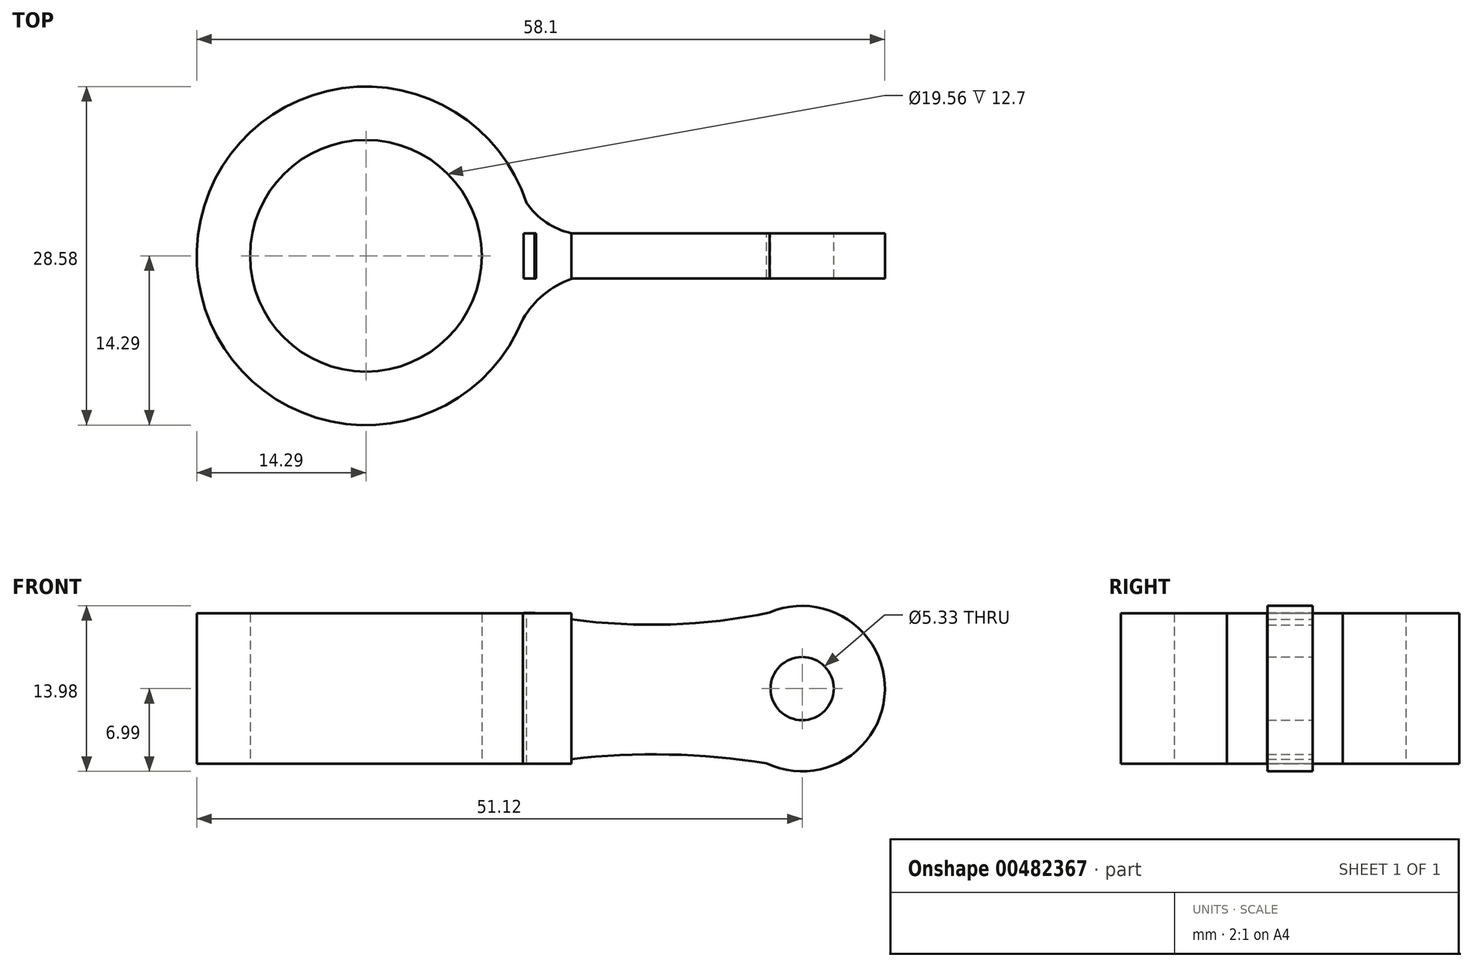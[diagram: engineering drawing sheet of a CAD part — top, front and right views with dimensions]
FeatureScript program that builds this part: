
annotation { "Feature Type Name" : "Feature", "Feature Type Description" : "" }
export const myFeature = defineFeature(function(context is Context, id is Id, definition is map)
    precondition{}
    {
        {
            var Q0;
            Q0=qCreatedBy(makeId("Top.planeOp"),FACE);
            var sketch = newSketch(context, id + "F0", { "sketchPlane" : qUnion([Q0])});
            skCircle(sketch, "E0", {"center": v(0, 0) * mm, "radius": 9.78 * mm});
            skCircle(sketch, "E1", {"center": v(0, 0) * mm, "radius": 14.29 * mm});
            skSolve(sketch);
        }
        {
            var Q0;
            Q0=makeQuery(id+"F0.imprint","IMPRINT",FACE,{"disambiguationData":[TD([[makeQuery(id+"F0.imprint","IMPRINT",EDGE,{"derivedFrom":sQuery(id+"F0.wireOp",EDGE,"E0")}),-1.0]])]});
            extrude(context, id + "F1", {"entities" : qUnion([Q0]), "depth" : 12.7 * mm});
        }
        {
            var Q0;
            Q0=qCreatedBy(makeId("Front.planeOp"),FACE);
            var sketch = newSketch(context, id + "F2", { "sketchPlane" : qUnion([Q0])});
            skLineSegment(sketch, "E2", {"start": v(0, 0) * mm, "end": v(0, 6.35) * mm});
            skLineSegment(sketch, "E3", {"start": v(0, 6.35) * mm, "end": v(36.83, 6.35) * mm});
            skCircle(sketch, "E4", {"center": v(36.83, 6.35) * mm, "radius": 2.67 * mm});
            skCircle(sketch, "E5", {"center": v(36.83, 6.35) * mm, "radius": 6.99 * mm});
            skArc(sketch, "E6", {"start": v(14.25, 12.72) * mm, "mid": v(25.39, 11.75) * mm, "end": v(36.46, 13.33) * mm});
            skArc(sketch, "E7", {"start": v(37.31, -0.62) * mm, "mid": v(25.97, 0.77) * mm, "end": v(14.57, 0) * mm});
            skLineSegment(sketch, "E8", {"start": v(14.57, 0) * mm, "end": v(13.31, 0) * mm});
            skLineSegment(sketch, "E9", {"start": v(13.31, 0) * mm, "end": v(13.31, 12.72) * mm});
            skLineSegment(sketch, "E10", {"start": v(13.31, 12.72) * mm, "end": v(14.25, 12.72) * mm});
            skSolve(sketch);
        }
        {
            var Q0;
            Q0 = qSketchRegion(id + "F2", true);
            extrude(context, id + "F3", {"entities" : qUnion([Q0]), "operationType" : NewBodyOperationType.ADD, "depth" : 1.9 * mm, "hasSecondDirection" : true, "secondDirectionOppositeDirection" : true, "secondDirectionDepth" : 1.9 * mm});
        }
        {
            var Q0;
            Q0=makeQuery(id+"F1.opExtrude","CAP_FACE",FACE,{"disambiguationData":[OSD([sQuery(id+"F0.wireOp",EDGE,"E0"),sQuery(id+"F0.wireOp",EDGE,"E1")])],"isStart":false});
            var sketch = newSketch(context, id + "F4", { "sketchPlane" : qUnion([Q0])});
            skLineSegment(sketch, "E11", {"start": v(-14.29, 0) * mm, "end": v(44.02, 0) * mm});
            skArc(sketch, "E12", {"start": v(17.34, -1.94) * mm, "mid": v(15, -3.29) * mm, "end": v(13.26, -5.33) * mm});
            skLineSegment(sketch, "E13", {"start": v(17.34, -1.94) * mm, "end": v(17.34, 1.9) * mm});
            skArc(sketch, "E14", {"start": v(13.58, 4.45) * mm, "mid": v(15.22, 2.82) * mm, "end": v(17.34, 1.9) * mm});
            skLineSegment(sketch, "E15", {"start": v(13.58, 4.45) * mm, "end": v(13.26, -5.33) * mm});
            skSolve(sketch);
        }
        {
            var Q0;
            {var subQ6=sQuery(id+"F4.wireOp",EDGE,"E14");Q0=makeQuery(id+"F4.imprint","IMPRINT",FACE,{"disambiguationData":[TD([[makeQuery(id+"F4.imprint","IMPRINT",EDGE,{"derivedFrom":subQ6}),-1.0]])]});}
            var Q1;
            {var subQ7=sQuery(id+"F4.wireOp",EDGE,"E12");Q1=makeQuery(id+"F4.imprint","IMPRINT",FACE,{"disambiguationData":[TD([[makeQuery(id+"F4.imprint","IMPRINT",EDGE,{"derivedFrom":subQ7}),-1.0]])]});}
            var Q2;
            Q2=makeQuery(id+"F3.boolean.opBoolean","MERGE",FACE,{"derivedFrom":[makeQuery(id+"F1.opExtrude","CAP_FACE",FACE,{"disambiguationData":[OSD([sQuery(id+"F0.wireOp",EDGE,"E0"),sQuery(id+"F0.wireOp",EDGE,"E1")])],"isStart":true}),makeQuery(id+"F3.opExtrude","SWEPT_FACE",FACE,{"disambiguationData":[OSD([sQuery(id+"F2.wireOp",EDGE,"E8")])]})]});
            extrude(context, id + "F5", {"entities" : qUnion([Q0, Q1]), "operationType" : NewBodyOperationType.ADD, "endBound" : BoundingType.UP_TO_SURFACE, "oppositeDirection" : true, "endBoundEntityFace" : qUnion([Q2]), "depth" : 25.4 * mm});
        }
    });
